# Revit family: Multibrand_Prosys_R0146_BIM_NN
name_source: partatom
category: Plumbing Fixtures
revit_build: Autodesk Revit 2017 (Build: 20160225_1515(x64)
units: mm (PartAtom-declared; Revit-internal decimal feet)

## family parameters
Always vertical = Yes
Cut with Voids When Loaded = No
OmniClass Number = 23.45.00.00
OmniClass Title = Sanitary, Laundry, and Cleaning Equipment
Part Type = Normal
Room Calculation Point = No
Round Connector Dimension = Use Radius
Shared = No
Work Plane-Based = No

## types (1)
- R014667 - Wet WC 74 (Simflex) CL1
    CISTERN_Height = 576 mm  [stored 1.88976 ft]
    CISTERN_Length = 458 mm  [stored 1.50262 ft]
    CISTERN_Material = PP
    CISTERN_Refill (sifónico) = NO
    CISTERN_Width = 80 mm  [stored 0.262467 ft]
    Description = Wet WC 74 (Simflex) CL1
    FRAME_Height = 780 mm  [stored 2.55906 ft]
    FRAME_Length = 460 mm  [stored 1.50919 ft]
    FRAME_Max Height = 780 mm  [stored 2.55906 ft]
    FRAME_Min Height = 780 mm  [stored 2.55906 ft]
    Material = FRAME_metal_cromo
    Model = R014667
    WATER CONNECTION_Diameter = 13 mm
    WATER CONNECTION_Flexible tube material = Stainless Steel Braided
    WATER CONNECTION_Position = TOP
    WATER CONNECTION_Waste pipe material = PP
    WATER CONNECTION_Waste pipe output = 110 mm  [stored 0.360892 ft]

note: [stored X ft] marks values corroborated as IEEE doubles in the binary element streams (Revit-internal decimal feet)

## geometry (parser evidence)
native form markers: Sweep x4
no freeform markers — native parametric forms only
